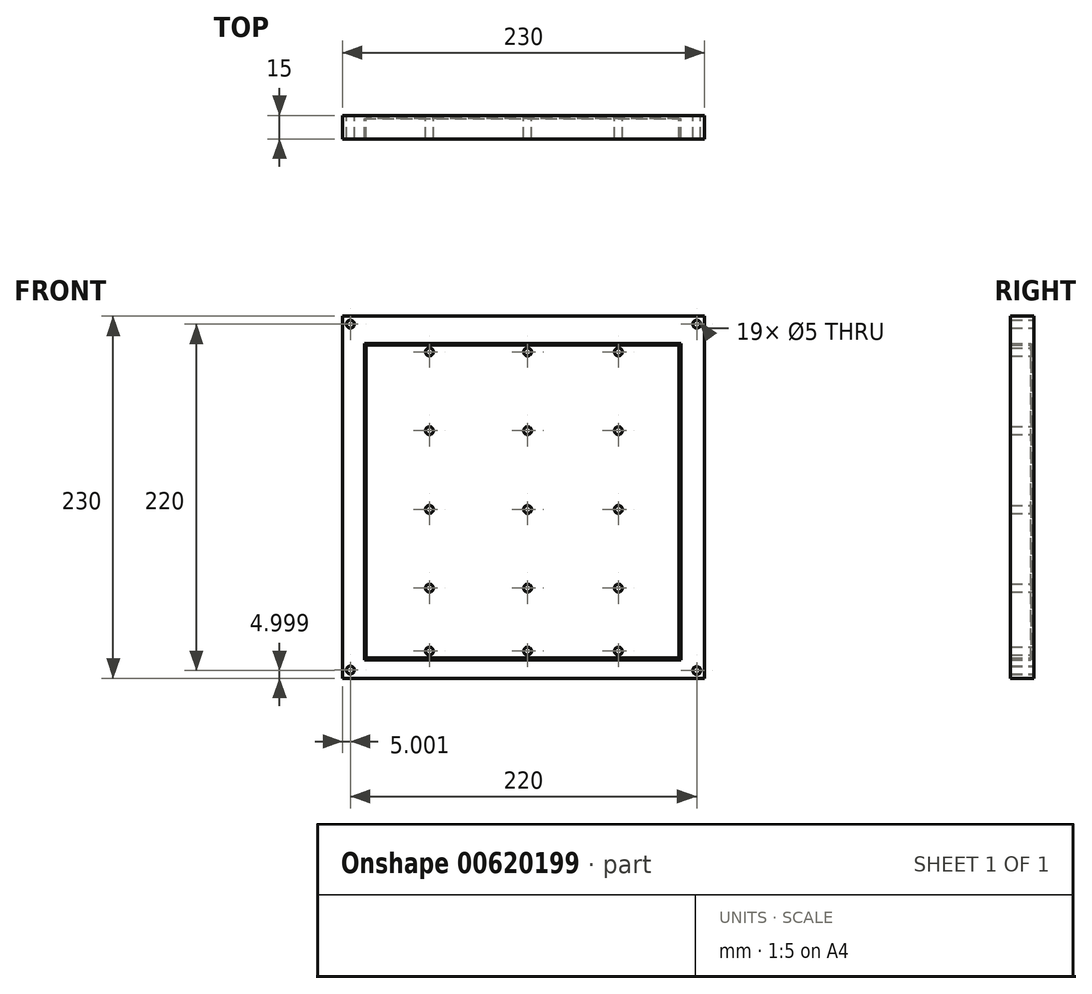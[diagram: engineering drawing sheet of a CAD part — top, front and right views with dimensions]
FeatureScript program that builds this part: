
annotation { "Feature Type Name" : "Feature", "Feature Type Description" : "" }
export const myFeature = defineFeature(function(context is Context, id is Id, definition is map)
    precondition{}
    {
        {
            var Q0;
            Q0=qCreatedBy(makeId("Front.planeOp"),FACE);
            var sketch = newSketch(context, id + "F0", { "sketchPlane" : qUnion([Q0])});
            skLineSegment(sketch, "E0.bottom", {"start": v(-117.54, 229.73) * mm, "end": v(112.46, 229.73) * mm});
            skLineSegment(sketch, "E0.top", {"start": v(-117.54, -0.27) * mm, "end": v(112.46, -0.27) * mm});
            skLineSegment(sketch, "E0.left", {"start": v(-117.54, 229.73) * mm, "end": v(-117.54, -0.27) * mm});
            skLineSegment(sketch, "E0.right", {"start": v(112.46, 229.73) * mm, "end": v(112.46, -0.27) * mm});
            skCircle(sketch, "E1", {"center": v(-62.3, 207.04) * mm, "radius": 2.5 * mm});
            skCircle(sketch, "E2", {"center": v(57.7, 207.04) * mm, "radius": 2.5 * mm});
            skCircle(sketch, "E3", {"center": v(0, 207.04) * mm, "radius": 2.5 * mm});
            skPoint(sketch, "E4.endSnap0", {"position": v(-3.18, 212.04) * mm});
            skCircle(sketch, "E5", {"center": v(-62.3, 157.04) * mm, "radius": 2.5 * mm});
            skCircle(sketch, "E6", {"center": v(-62.3, 107.04) * mm, "radius": 2.5 * mm});
            skCircle(sketch, "E7", {"center": v(-62.3, 57.04) * mm, "radius": 2.5 * mm});
            skCircle(sketch, "E8", {"center": v(-62.3, 17.04) * mm, "radius": 2.5 * mm});
            skCircle(sketch, "E9", {"center": v(0, 157.04) * mm, "radius": 2.5 * mm});
            skCircle(sketch, "E10", {"center": v(57.7, 157.04) * mm, "radius": 2.5 * mm});
            skCircle(sketch, "E11", {"center": v(0, 107.04) * mm, "radius": 2.5 * mm});
            skCircle(sketch, "E12", {"center": v(57.7, 107.04) * mm, "radius": 2.5 * mm});
            skCircle(sketch, "E13", {"center": v(0, 57.04) * mm, "radius": 2.5 * mm});
            skCircle(sketch, "E14", {"center": v(57.7, 57.04) * mm, "radius": 2.5 * mm});
            skCircle(sketch, "E15", {"center": v(0, 17.04) * mm, "radius": 2.5 * mm});
            skCircle(sketch, "E16", {"center": v(57.7, 17.04) * mm, "radius": 2.5 * mm});
            skPoint(sketch, "E17", {"position": v(-103.68, 212.54) * mm});
            skPoint(sketch, "E18", {"position": v(97.32, 11.54) * mm});
            skLineSegment(sketch, "E19.bottom", {"start": v(-103.68, 212.54) * mm, "end": v(97.32, 212.54) * mm});
            skLineSegment(sketch, "E19.top", {"start": v(-103.68, 11.54) * mm, "end": v(97.32, 11.54) * mm});
            skLineSegment(sketch, "E19.left", {"start": v(-103.68, 212.54) * mm, "end": v(-103.68, 11.54) * mm});
            skLineSegment(sketch, "E19.right", {"start": v(97.32, 212.54) * mm, "end": v(97.32, 11.54) * mm});
            skPoint(sketch, "E20", {"position": v(-102.68, 211.54) * mm});
            skPoint(sketch, "E21", {"position": v(96.32, 12.54) * mm});
            skLineSegment(sketch, "E22.bottom", {"start": v(96.32, 12.54) * mm, "end": v(-102.68, 12.54) * mm});
            skLineSegment(sketch, "E22.top", {"start": v(96.32, 211.54) * mm, "end": v(-102.68, 211.54) * mm});
            skLineSegment(sketch, "E22.left", {"start": v(96.32, 12.54) * mm, "end": v(96.32, 211.54) * mm});
            skLineSegment(sketch, "E22.right", {"start": v(-102.68, 12.54) * mm, "end": v(-102.68, 211.54) * mm});
            skPoint(sketch, "E23", {"position": v(-112.54, 224.73) * mm});
            skCircle(sketch, "E24", {"center": v(-112.54, 224.73) * mm, "radius": 2.5 * mm});
            skCircle(sketch, "E25", {"center": v(107.46, 224.73) * mm, "radius": 2.5 * mm});
            skCircle(sketch, "E26", {"center": v(107.46, 4.73) * mm, "radius": 2.5 * mm});
            skCircle(sketch, "E27", {"center": v(-112.54, 5) * mm, "radius": 2.5 * mm});
            skSolve(sketch);
        }
        {
            var Q0;
            Q0=makeQuery(id+"F0.imprint","IMPRINT",FACE,{"disambiguationData":[TD([[makeQuery(id+"F0.imprint","IMPRINT",EDGE,{"derivedFrom":sQuery(id+"F0.wireOp",EDGE,"E19.bottom")}),-1.0]])]});
            extrude(context, id + "F1", {"entities" : qUnion([Q0]), "depth" : 2 * mm, "offsetDistance" : 25 * mm});
        }
        {
            var Q0;
            Q0=makeQuery(id+"F0.imprint","IMPRINT",FACE,{"disambiguationData":[TD([[makeQuery(id+"F0.imprint","IMPRINT",EDGE,{"derivedFrom":sQuery(id+"F0.wireOp",EDGE,"E0.bottom")}),-1.0]])]});
            var Q1;
            Q1=makeQuery(id+"F0.imprint","IMPRINT",FACE,{"disambiguationData":[TD([[makeQuery(id+"F0.imprint","IMPRINT",EDGE,{"derivedFrom":sQuery(id+"F0.wireOp",EDGE,"E1")}),-1.0]])]});
            extrude(context, id + "F2", {"entities" : qUnion([Q0, Q1]), "operationType" : NewBodyOperationType.ADD, "depth" : 15 * mm, "offsetDistance" : 25 * mm});
        }
    });
